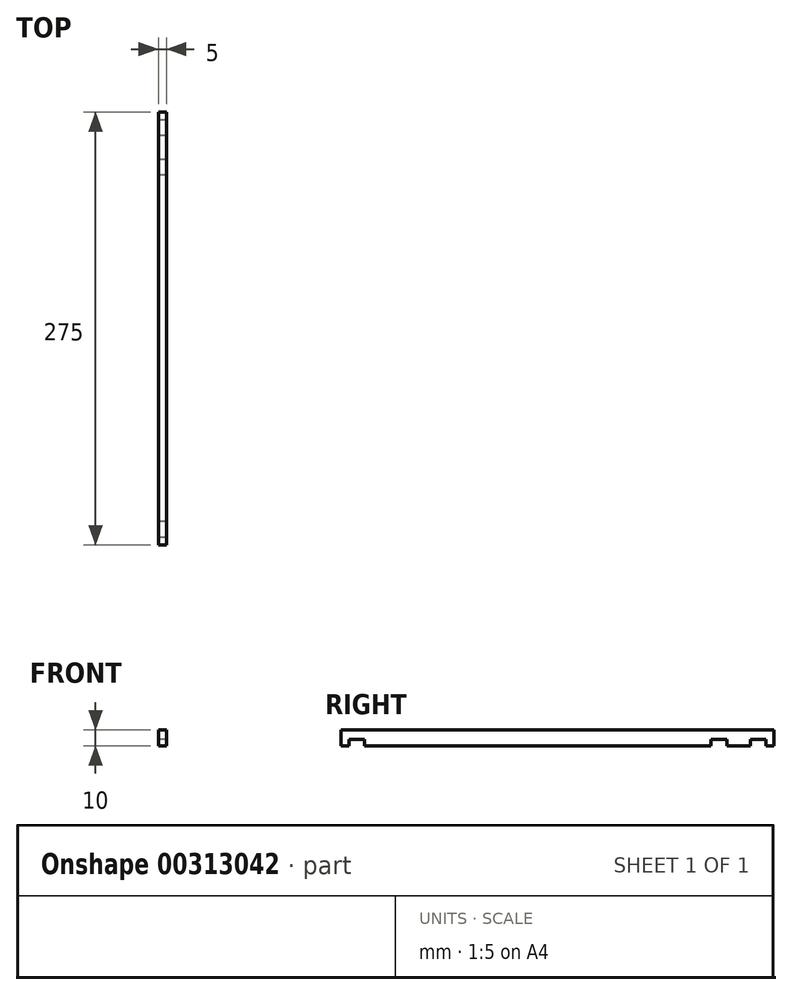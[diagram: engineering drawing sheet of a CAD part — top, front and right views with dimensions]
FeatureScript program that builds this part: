
annotation { "Feature Type Name" : "Feature", "Feature Type Description" : "" }
export const myFeature = defineFeature(function(context is Context, id is Id, definition is map)
    precondition{}
    {
        {
            var Q0;
            Q0=qCreatedBy(makeId("Right.planeOp"),FACE);
            var sketch = newSketch(context, id + "F0", { "sketchPlane" : qUnion([Q0])});
            skLineSegment(sketch, "E0", {"start": v(-111.06, 0) * mm, "end": v(108.94, 0) * mm});
            skLineSegment(sketch, "E1", {"start": v(-111.06, 0) * mm, "end": v(-111.06, 4) * mm});
            skLineSegment(sketch, "E2", {"start": v(-111.06, 4) * mm, "end": v(-121.06, 4) * mm});
            skLineSegment(sketch, "E3", {"start": v(-121.06, 4) * mm, "end": v(-121.06, 0) * mm});
            skLineSegment(sketch, "E4", {"start": v(-121.06, 0) * mm, "end": v(-126.06, 0) * mm});
            skLineSegment(sketch, "E5", {"start": v(-126.06, 0) * mm, "end": v(-126.06, 10) * mm});
            skLineSegment(sketch, "E6", {"start": v(-126.06, 10) * mm, "end": v(148.94, 10) * mm});
            skLineSegment(sketch, "E7", {"start": v(148.94, 10) * mm, "end": v(148.94, 0) * mm});
            skLineSegment(sketch, "E8", {"start": v(148.94, 0) * mm, "end": v(143.94, 0) * mm});
            skLineSegment(sketch, "E9", {"start": v(118.94, 0) * mm, "end": v(118.94, 4) * mm});
            skLineSegment(sketch, "E10", {"start": v(118.94, 4) * mm, "end": v(108.94, 4) * mm});
            skLineSegment(sketch, "E11", {"start": v(108.94, 4) * mm, "end": v(108.94, 0) * mm});
            skLineSegment(sketch, "E12", {"start": v(118.94, 0) * mm, "end": v(133.94, 0) * mm, "construction": true});
            skLineSegment(sketch, "E13", {"start": v(133.94, 0) * mm, "end": v(133.94, 4) * mm});
            skLineSegment(sketch, "E14", {"start": v(133.94, 4) * mm, "end": v(143.94, 4) * mm});
            skLineSegment(sketch, "E15", {"start": v(143.94, 4) * mm, "end": v(143.94, 0) * mm});
            skLineSegment(sketch, "E16.trimOffspring", {"start": v(133.94, 0) * mm, "end": v(118.94, 0) * mm});
            skSolve(sketch);
        }
        {
            var Q0;
            Q0=makeQuery(id+"F0.imprint","IMPRINT",FACE,{"disambiguationData":[TD([[makeQuery(id+"F0.imprint","IMPRINT",EDGE,{"derivedFrom":sQuery(id+"F0.wireOp",EDGE,"E0")}),1.0]])]});
            extrude(context, id + "F1", {"entities" : qUnion([Q0]), "depth" : 5 * mm});
        }
    });
